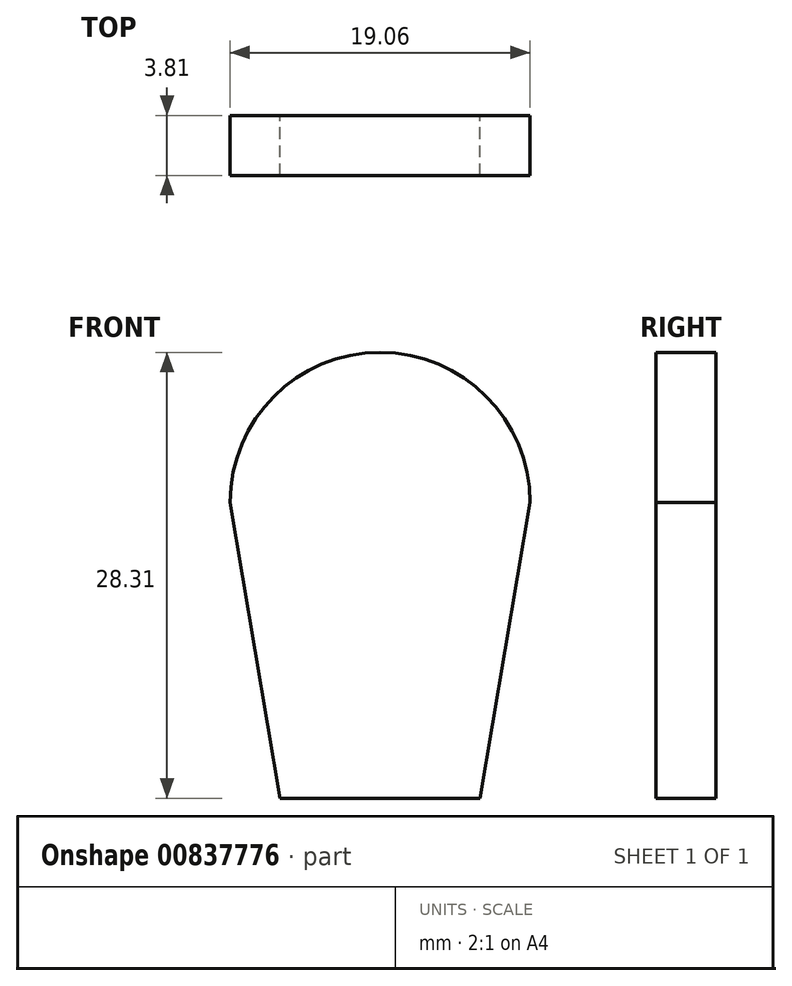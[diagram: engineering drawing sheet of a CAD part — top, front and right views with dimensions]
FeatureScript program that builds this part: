
annotation { "Feature Type Name" : "Feature", "Feature Type Description" : "" }
export const myFeature = defineFeature(function(context is Context, id is Id, definition is map)
    precondition{}
    {
        {
            var Q0;
            Q0=qCreatedBy(makeId("Front.planeOp"),FACE);
            var sketch = newSketch(context, id + "F0", { "sketchPlane" : qUnion([Q0])});
            skLineSegment(sketch, "E0", {"start": v(0, 0) * mm, "end": v(6.35, 0) * mm});
            skLineSegment(sketch, "E1", {"start": v(6.35, 0) * mm, "end": v(9.53, 18.78) * mm});
            skLineSegment(sketch, "E2", {"start": v(9.52, 18.78) * mm, "end": v(-9.53, 18.78) * mm});
            skLineSegment(sketch, "E3", {"start": v(-9.52, 18.78) * mm, "end": v(-6.35, 0) * mm});
            skLineSegment(sketch, "E4", {"start": v(-6.35, 0) * mm, "end": v(0, 0) * mm});
            skArc(sketch, "E5", {"start": v(-9.53, 18.78) * mm, "mid": v(0, 28.3) * mm, "end": v(9.52, 18.78) * mm});
            skSolve(sketch);
        }
        {
            var Q0;
            Q0=makeQuery(id+"F0.imprint","IMPRINT",FACE,{"disambiguationData":[TD([[makeQuery(id+"F0.imprint","IMPRINT",EDGE,{"derivedFrom":sQuery(id+"F0.wireOp",EDGE,"E0")}),1.0]])]});
            extrude(context, id + "F1", {"entities" : qUnion([Q0]), "depth" : 3.8 * mm, "offsetDistance" : 25.4 * mm});
        }
        {
            var Q0;
            Q0=makeQuery(id+"F0.imprint","IMPRINT",FACE,{"disambiguationData":[TD([[makeQuery(id+"F0.imprint","IMPRINT",EDGE,{"derivedFrom":sQuery(id+"F0.wireOp",EDGE,"E2")}),-1.0]])]});
            extrude(context, id + "F2", {"entities" : qUnion([Q0]), "operationType" : NewBodyOperationType.ADD, "depth" : 3.8 * mm, "offsetDistance" : 25.4 * mm});
        }
    });
